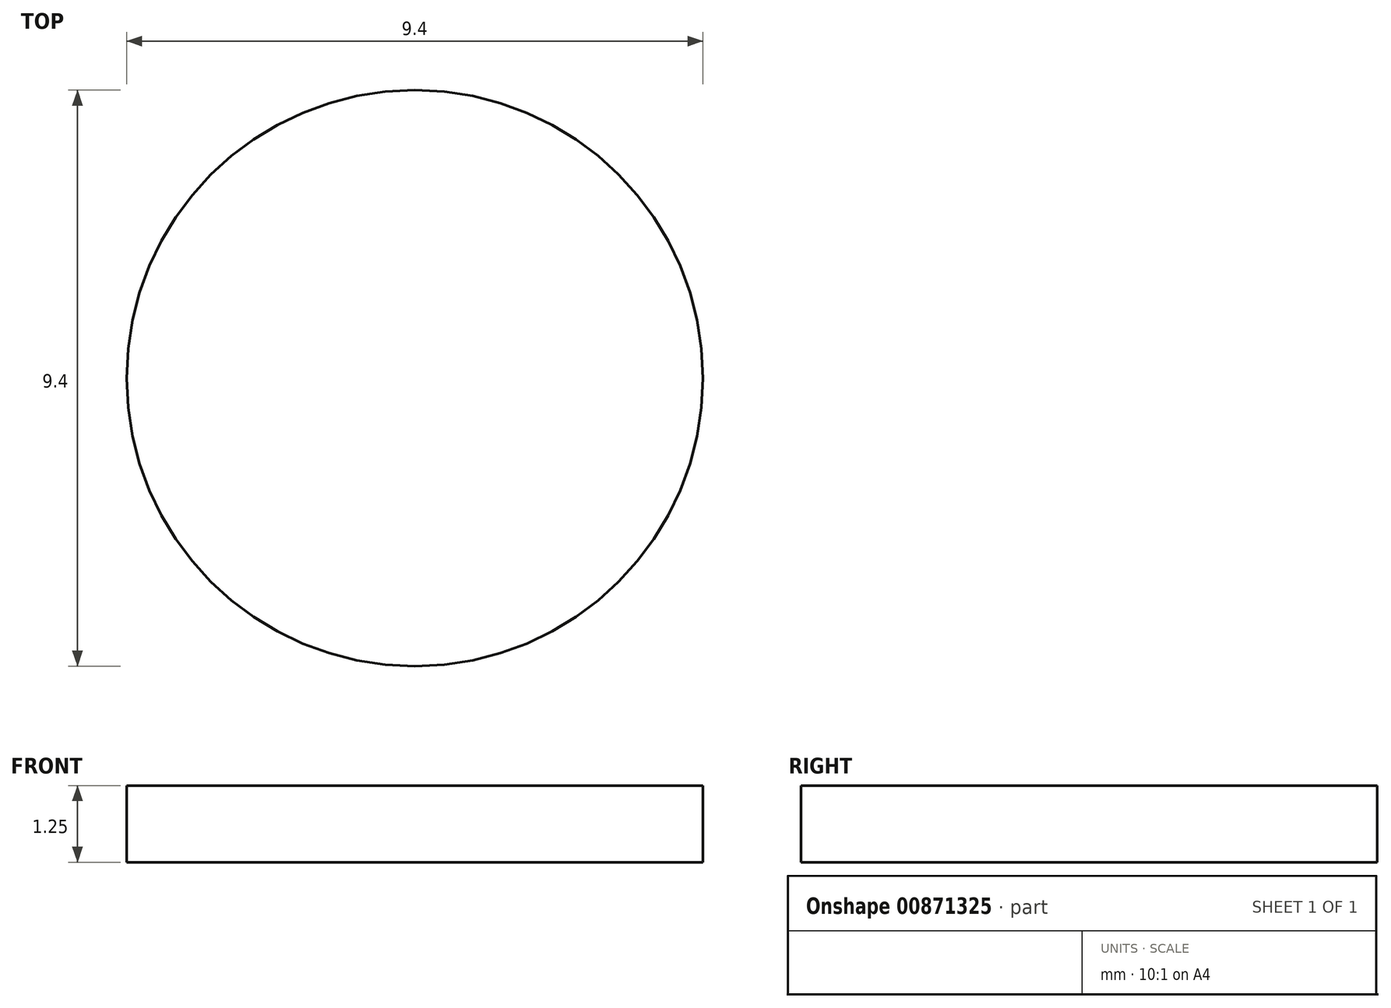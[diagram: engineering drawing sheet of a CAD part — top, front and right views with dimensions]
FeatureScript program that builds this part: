
annotation { "Feature Type Name" : "Feature", "Feature Type Description" : "" }
export const myFeature = defineFeature(function(context is Context, id is Id, definition is map)
    precondition{}
    {
        {
            var Q0;
            Q0=qCreatedBy(makeId("Top.planeOp"),FACE);
            var sketch = newSketch(context, id + "F0", { "sketchPlane" : qUnion([Q0])});
            skCircle(sketch, "E0", {"center": v(0, 0) * mm, "radius": 4.7 * mm});
            skSolve(sketch);
        }
        {
            var Q0;
            Q0=makeQuery(id+"F0.imprint","IMPRINT",FACE,{"disambiguationData":[TD([[makeQuery(id+"F0.imprint","IMPRINT",EDGE,{"derivedFrom":sQuery(id+"F0.wireOp",EDGE,"E0")}),1.0]])]});
            extrude(context, id + "F1", {"entities" : qUnion([Q0]), "depth" : 1.25 * mm, "offsetDistance" : 25 * mm});
        }
    });
